# Revit family: SANINDUSA_109760004_Flux_80x45FluxWallMountedBasin80x45_V0
name_source: partatom
category: Plumbing Fixtures
units: mm (PartAtom-declared; Revit-internal decimal feet)

## family parameters
Cut with Voids When Loaded = No
Host = Face
Part Type = Normal
Room Calculation Point = No
Round Connector Dimension = Use Diameter
Shared = No

## types (1)
- SANINDUSA_109760004_Flux_80x45FluxWallMountedBasin80x45_V0
    AssetType = Fixed
    CodePerformance = EN 14688:2006  CL 00
    Color = white
    Constituents = Siphon adapter ref. 4V9811 included
    Default Elevation = 0 mm  [stored 0 ft]
    Description = Wastewater appliance for washing the upper parts of the body.
    DrainSize = 45 mm  [stored 0.147638 ft]
    Element Type = WASHHANDBASIN: Waste water appliance for washing the upper parts of the body.
    Features = Installation wall-mounted, Without overflow. Compatible with Fixing kit 43, included.
    Finish = gloss
    Installation Instructions = https://www.tec.sanindusa.pt
    InstallationDate = 1900-12-31T23:59:59
    Manufacturer = Sanindusa
    ManufacturerName = Sanindusa
    ManufacturerURL = www.tec.sanindusa.pt
    Material = vitreous china
    Model = 109760004
    ModelNumber = 109760004
    ModelReference = Flux
    Name = 80x45 Flux basin
    NominalDepth = 85 mm  [stored 0.278871 ft]
    NominalHeight = 135 mm  [stored 0.442913 ft]
    NominalLength = 800 mm  [stored 2.62467 ft]
    NominalWidth = 450 mm  [stored 1.47638 ft]
    Pre-defined type (IFC) = WASHHANDBASIN
    ProductInformation = https://www.tec.sanindusa.pt
    ProductionYear = 2005
    Shape = rectangular
    Size = 80x45
    Type (IFC) = IfcSanitaryTerminalType
    URL = www.tec.sanindusa.pt
    Uniclass2015Code = Pr_40_20_96_18
    Uniclass2015Title = Counter top wash basins
    Uniclass2015Version = Products v1.6
    Version = 1
    WarrantyDescription = https://www.tec.sanindusa.pt
    WarrantyDurationParts = 5
    WarrantyDurationUnit = year
    WarrantyStartDate = 1900-12-31T23:59:59
    WashHandBasinMounting = wallhung
    WashHandBasinType = handrinse
    Waste Connection = Yes
    Weight = 19.00 kg

note: [stored X ft] marks values corroborated as IEEE doubles in the binary element streams (Revit-internal decimal feet)

## geometry (parser evidence)
native form markers: Sweep x8
no freeform markers — native parametric forms only
